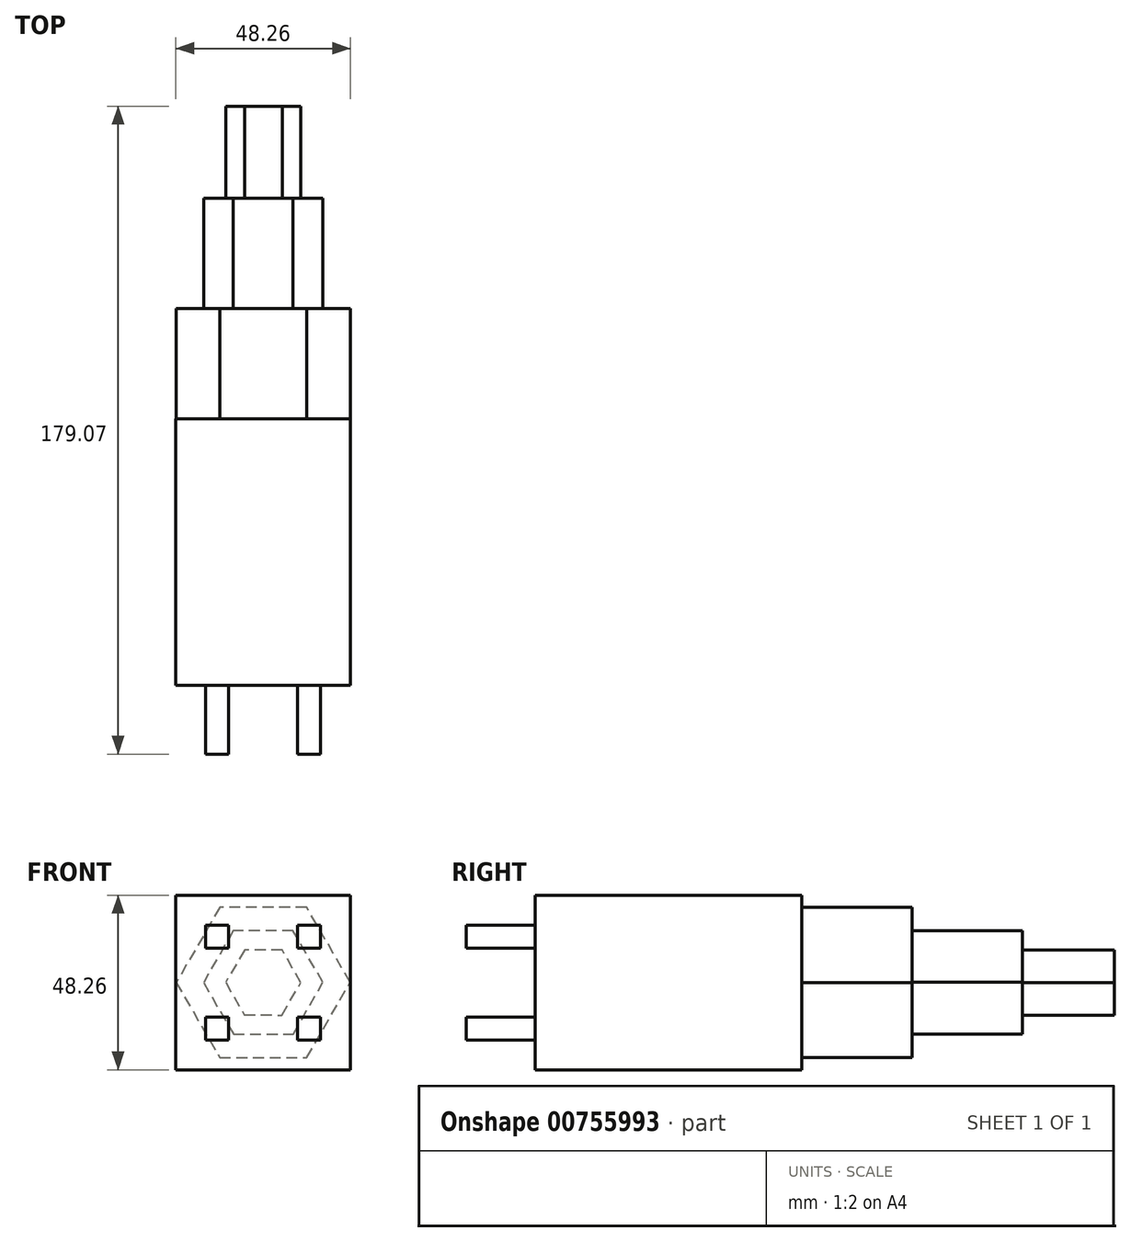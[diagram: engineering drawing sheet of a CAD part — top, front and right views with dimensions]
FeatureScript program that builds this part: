
annotation { "Feature Type Name" : "Feature", "Feature Type Description" : "" }
export const myFeature = defineFeature(function(context is Context, id is Id, definition is map)
    precondition{}
    {
        {
            var Q0;
            Q0=qCreatedBy(makeId("Top.planeOp"),FACE);
            var sketch = newSketch(context, id + "F0", { "sketchPlane" : qUnion([Q0])});
            skLineSegment(sketch, "E0.bottom", {"start": v(0, 0) * mm, "end": v(48.26, 0) * mm});
            skLineSegment(sketch, "E0.top", {"start": v(0, 73.66) * mm, "end": v(48.26, 73.66) * mm});
            skLineSegment(sketch, "E0.left", {"start": v(0, 0) * mm, "end": v(0, 73.66) * mm});
            skLineSegment(sketch, "E0.right", {"start": v(48.26, 0) * mm, "end": v(48.26, 73.66) * mm});
            skSolve(sketch);
        }
        {
            var Q0;
            Q0 = qSketchRegion(id + "F0", true);
            extrude(context, id + "F1", {"entities" : qUnion([Q0]), "depth" : 48.26 * mm, "offsetDistance" : 25.4 * mm});
        }
        {
            var Q0;
            Q0=makeQuery(id+"F1.opExtrude","SWEPT_FACE",FACE,{"disambiguationData":[OSD([sQuery(id+"F0.wireOp",EDGE,"E0.top")])]});
            var sketch = newSketch(context, id + "F2", { "sketchPlane" : qUnion([Q0])});
            skLineSegment(sketch, "E1", {"start": v(-24.13, 48.26) * mm, "end": v(-24.13, 9.05) * mm});
            skLineSegment(sketch, "E2", {"start": v(-24.13, 9.05) * mm, "end": v(-48.26, 24.13) * mm});
            skLineSegment(sketch, "E3", {"start": v(-48.26, 24.13) * mm, "end": v(-11.74, 24.13) * mm});
            skCircle(sketch, "E4.cCircle", {"center": v(-24.13, 24.13) * mm, "radius": 20.8 * mm, "construction": true});
            skLineSegment(sketch, "E4.0", {"start": v(-36.14, 44.93) * mm, "end": v(-12.12, 44.93) * mm});
            skLineSegment(sketch, "E4.1", {"start": v(-12.12, 44.93) * mm, "end": v(-0.11, 24.13) * mm});
            skLineSegment(sketch, "E4.2", {"start": v(-0.11, 24.13) * mm, "end": v(-12.12, 3.33) * mm});
            skLineSegment(sketch, "E4.3", {"start": v(-12.12, 3.33) * mm, "end": v(-36.14, 3.33) * mm});
            skLineSegment(sketch, "E4.4", {"start": v(-36.14, 3.33) * mm, "end": v(-48.15, 24.13) * mm});
            skLineSegment(sketch, "E4.5", {"start": v(-48.15, 24.13) * mm, "end": v(-36.14, 44.93) * mm});
            skPoint(sketch, "E4.0.midPoint", {"position": v(-24.13, 44.93) * mm});
            skSolve(sketch);
        }
        {
            var Q0;
            Q0 = qSketchRegion(id + "F2", true);
            extrude(context, id + "F3", {"entities" : qUnion([Q0]), "operationType" : NewBodyOperationType.ADD, "depth" : 30.48 * mm, "offsetDistance" : 25.4 * mm});
        }
        {
            var Q0;
            Q0=makeQuery(id+"F3.opExtrude","CAP_FACE",FACE,{"disambiguationData":[OSD([sQuery(id+"F2.wireOp",EDGE,"E2"),sQuery(id+"F2.wireOp",EDGE,"E3"),sQuery(id+"F2.wireOp",EDGE,"E4.0"),sQuery(id+"F2.wireOp",EDGE,"E4.1"),sQuery(id+"F2.wireOp",EDGE,"E4.2"),sQuery(id+"F2.wireOp",EDGE,"E4.3"),sQuery(id+"F2.wireOp",EDGE,"E4.4"),sQuery(id+"F2.wireOp",EDGE,"E4.5")])],"isStart":false});
            var sketch = newSketch(context, id + "F4", { "sketchPlane" : qUnion([Q0])});
            skLineSegment(sketch, "E5", {"start": v(-24.13, 44.93) * mm, "end": v(-24.13, 3.33) * mm});
            skLineSegment(sketch, "E6", {"start": v(-48.09, 24.02) * mm, "end": v(-2.31, 24.13) * mm});
            skCircle(sketch, "E7.cCircle", {"center": v(-24.13, 24.13) * mm, "radius": 14.3 * mm, "construction": true});
            skLineSegment(sketch, "E7.0", {"start": v(-15.87, 38.41) * mm, "end": v(-7.63, 24.11) * mm});
            skLineSegment(sketch, "E7.1", {"start": v(-7.63, 24.11) * mm, "end": v(-15.9, 9.83) * mm});
            skLineSegment(sketch, "E7.2", {"start": v(-15.9, 9.83) * mm, "end": v(-32.4, 9.85) * mm});
            skLineSegment(sketch, "E7.3", {"start": v(-32.4, 9.85) * mm, "end": v(-40.63, 24.15) * mm});
            skLineSegment(sketch, "E7.4", {"start": v(-40.63, 24.15) * mm, "end": v(-32.37, 38.43) * mm});
            skLineSegment(sketch, "E7.5", {"start": v(-32.37, 38.43) * mm, "end": v(-15.87, 38.41) * mm});
            skPoint(sketch, "E7.0.midPoint", {"position": v(-11.75, 31.26) * mm});
            skSolve(sketch);
        }
        {
            var Q0;
            Q0 = qSketchRegion(id + "F4", true);
            extrude(context, id + "F5", {"entities" : qUnion([Q0]), "operationType" : NewBodyOperationType.ADD, "depth" : 30.48 * mm, "offsetDistance" : 25.4 * mm});
        }
        {
            var Q0;
            Q0=makeQuery(id+"F5.opExtrude","CAP_FACE",FACE,{"disambiguationData":[OSD([sQuery(id+"F4.wireOp",EDGE,"E7.0"),sQuery(id+"F4.wireOp",EDGE,"E7.1"),sQuery(id+"F4.wireOp",EDGE,"E7.2"),sQuery(id+"F4.wireOp",EDGE,"E7.3"),sQuery(id+"F4.wireOp",EDGE,"E7.4"),sQuery(id+"F4.wireOp",EDGE,"E7.5")])],"isStart":false});
            var sketch = newSketch(context, id + "F6", { "sketchPlane" : qUnion([Q0])});
            skLineSegment(sketch, "E8", {"start": v(-24.12, 38.42) * mm, "end": v(-24.12, 9.84) * mm});
            skLineSegment(sketch, "E9", {"start": v(-40.63, 24.15) * mm, "end": v(-7.63, 24.11) * mm});
            skCircle(sketch, "E10.cCircle", {"center": v(-24.13, 24.13) * mm, "radius": 9 * mm, "construction": true});
            skLineSegment(sketch, "E10.0", {"start": v(-19, 33.15) * mm, "end": v(-13.75, 24.2) * mm});
            skLineSegment(sketch, "E10.1", {"start": v(-13.75, 24.2) * mm, "end": v(-18.88, 15.17) * mm});
            skLineSegment(sketch, "E10.2", {"start": v(-18.88, 15.17) * mm, "end": v(-29.26, 15.1) * mm});
            skLineSegment(sketch, "E10.3", {"start": v(-29.26, 15.1) * mm, "end": v(-34.51, 24.06) * mm});
            skLineSegment(sketch, "E10.4", {"start": v(-34.51, 24.06) * mm, "end": v(-29.38, 33.09) * mm});
            skLineSegment(sketch, "E10.5", {"start": v(-29.38, 33.09) * mm, "end": v(-19, 33.15) * mm});
            skPoint(sketch, "E10.0.midPoint", {"position": v(-16.37, 28.67) * mm});
            skSolve(sketch);
        }
        {
            var Q0;
            Q0 = qSketchRegion(id + "F6", true);
            extrude(context, id + "F7", {"entities" : qUnion([Q0]), "operationType" : NewBodyOperationType.ADD, "depth" : 25.4 * mm, "offsetDistance" : 25.4 * mm});
        }
        {
            var Q0;
            Q0=makeQuery(id+"F1.opExtrude","SWEPT_FACE",FACE,{"disambiguationData":[OSD([sQuery(id+"F0.wireOp",EDGE,"E0.bottom")])]});
            var sketch = newSketch(context, id + "F8", { "sketchPlane" : qUnion([Q0])});
            skLineSegment(sketch, "E11", {"start": v(48.26, 48.26) * mm, "end": v(36.83, 48.26) * mm});
            skLineSegment(sketch, "E12", {"start": v(36.83, 48.26) * mm, "end": v(36.83, 36.83) * mm});
            skLineSegment(sketch, "E13", {"start": v(36.83, 36.83) * mm, "end": v(36.83, 11.43) * mm});
            skLineSegment(sketch, "E14", {"start": v(36.83, 11.43) * mm, "end": v(11.43, 11.43) * mm});
            skLineSegment(sketch, "E15", {"start": v(11.43, 11.43) * mm, "end": v(11.43, 36.83) * mm});
            skLineSegment(sketch, "E16.bottom", {"start": v(14.6, 40) * mm, "end": v(8.25, 40) * mm});
            skLineSegment(sketch, "E16.top", {"start": v(14.6, 33.66) * mm, "end": v(8.25, 33.66) * mm});
            skLineSegment(sketch, "E16.left", {"start": v(14.6, 40) * mm, "end": v(14.6, 33.66) * mm});
            skLineSegment(sketch, "E16.right", {"start": v(8.25, 40) * mm, "end": v(8.25, 33.66) * mm});
            skPoint(sketch, "E16.middle", {"position": v(11.43, 36.83) * mm});
            skPoint(sketch, "E17.middle", {"position": v(11.43, 11.43) * mm});
            skLineSegment(sketch, "E18.bottom", {"start": v(33.65, 14.6) * mm, "end": v(40, 14.6) * mm});
            skLineSegment(sketch, "E18.top", {"start": v(33.65, 8.26) * mm, "end": v(40, 8.26) * mm});
            skLineSegment(sketch, "E18.left", {"start": v(33.65, 14.6) * mm, "end": v(33.65, 8.26) * mm});
            skLineSegment(sketch, "E18.right", {"start": v(40, 14.6) * mm, "end": v(40, 8.26) * mm});
            skPoint(sketch, "E18.middle", {"position": v(36.83, 11.43) * mm});
            skLineSegment(sketch, "E19.bottom", {"start": v(33.65, 40) * mm, "end": v(40, 40) * mm});
            skLineSegment(sketch, "E19.top", {"start": v(33.65, 33.65) * mm, "end": v(40, 33.65) * mm});
            skLineSegment(sketch, "E19.left", {"start": v(33.65, 40) * mm, "end": v(33.65, 33.65) * mm});
            skLineSegment(sketch, "E19.right", {"start": v(40, 40) * mm, "end": v(40, 33.65) * mm});
            skPoint(sketch, "E19.middle", {"position": v(36.83, 36.83) * mm});
            skLineSegment(sketch, "E20.bottom", {"start": v(14.6, 14.6) * mm, "end": v(8.26, 14.6) * mm});
            skLineSegment(sketch, "E20.top", {"start": v(14.6, 8.25) * mm, "end": v(8.26, 8.25) * mm});
            skLineSegment(sketch, "E20.left", {"start": v(14.6, 14.6) * mm, "end": v(14.6, 8.25) * mm});
            skLineSegment(sketch, "E20.right", {"start": v(8.26, 14.6) * mm, "end": v(8.26, 8.25) * mm});
            skSolve(sketch);
        }
        {
            var Q0;
            {var subQ0=sQuery(id+"F8.wireOp",EDGE,"E19.right");Q0=makeQuery(id+"F8.imprint","IMPRINT",FACE,{"disambiguationData":[TD([[makeQuery(id+"F8.imprint","IMPRINT",EDGE,{"derivedFrom":subQ0}),-1.0]])]});}
            var Q1;
            {var subQ0=sQuery(id+"F8.wireOp",EDGE,"E19.left");Q1=makeQuery(id+"F8.imprint","IMPRINT",FACE,{"disambiguationData":[TD([[makeQuery(id+"F8.imprint","IMPRINT",EDGE,{"derivedFrom":subQ0}),1.0]])]});}
            var Q2;
            Q2=makeQuery(id+"F8.imprint","IMPRINT",FACE,{"disambiguationData":[TD([[makeQuery(id+"F8.imprint","IMPRINT",EDGE,{"derivedFrom":sQuery(id+"F8.wireOp",EDGE,"E16.bottom")}),1.0]])]});
            var Q3;
            {var subQ0=sQuery(id+"F8.wireOp",EDGE,"E20.top");Q3=makeQuery(id+"F8.imprint","IMPRINT",FACE,{"disambiguationData":[TD([[makeQuery(id+"F8.imprint","IMPRINT",EDGE,{"derivedFrom":subQ0}),-1.0]])]});}
            var Q4;
            {var subQ0=sQuery(id+"F8.wireOp",EDGE,"E15");var subQ1=sQuery(id+"F8.wireOp",EDGE,"E14");var subQ2=makeQuery(id+"F8.imprint","INTERSECT",VERTEX,{"derivedFrom":[subQ1,subQ0]});Q4=makeQuery(id+"F8.imprint","IMPRINT",FACE,{"disambiguationData":[TD([[makeQuery(id+"F8.imprint","IMPRINT",EDGE,{"disambiguationData":[TD([[subQ2,1.0]])],"derivedFrom":subQ1}),-1.0]])]});}
            var Q5;
            {var subQ0=sQuery(id+"F8.wireOp",EDGE,"E18.top");Q5=makeQuery(id+"F8.imprint","IMPRINT",FACE,{"disambiguationData":[TD([[makeQuery(id+"F8.imprint","IMPRINT",EDGE,{"derivedFrom":subQ0}),1.0]])]});}
            var Q6;
            {var subQ0=sQuery(id+"F8.wireOp",EDGE,"E14");var subQ1=sQuery(id+"F8.wireOp",EDGE,"E13");var subQ2=makeQuery(id+"F8.imprint","INTERSECT",VERTEX,{"derivedFrom":[subQ1,subQ0]});Q6=makeQuery(id+"F8.imprint","IMPRINT",FACE,{"disambiguationData":[TD([[makeQuery(id+"F8.imprint","IMPRINT",EDGE,{"disambiguationData":[TD([[subQ2,1.0]])],"derivedFrom":subQ1}),-1.0]])]});}
            extrude(context, id + "F9", {"entities" : qUnion([Q0, Q1, Q2, Q3, Q4, Q5, Q6]), "operationType" : NewBodyOperationType.ADD, "depth" : 19.05 * mm, "offsetDistance" : 25.4 * mm});
        }
    });
